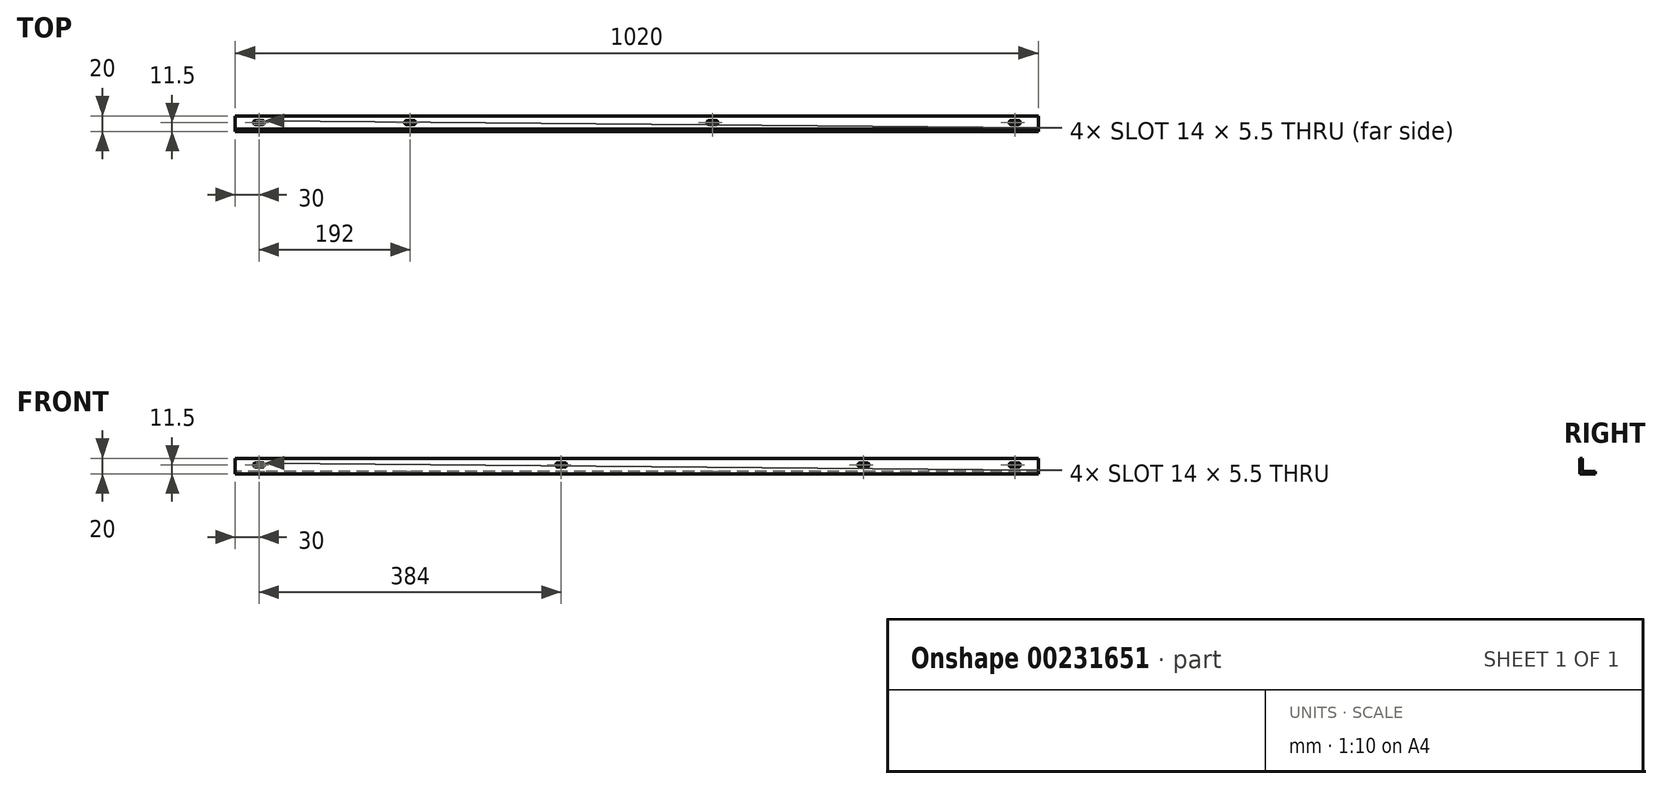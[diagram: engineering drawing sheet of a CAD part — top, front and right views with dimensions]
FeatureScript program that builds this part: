
annotation { "Feature Type Name" : "Feature", "Feature Type Description" : "" }
export const myFeature = defineFeature(function(context is Context, id is Id, definition is map)
    precondition{}
    {
        {
            var Q0;
            Q0=qCreatedBy(makeId("Right.planeOp"),FACE);
            var sketch = newSketch(context, id + "F0", { "sketchPlane" : qUnion([Q0])});
            skLineSegment(sketch, "E0.bottom", {"start": v(0, 0) * mm, "end": v(20, 0) * mm});
            skLineSegment(sketch, "E0.top", {"start": v(3, 3) * mm, "end": v(20, 3) * mm});
            skLineSegment(sketch, "E0.right", {"start": v(20, 0) * mm, "end": v(20, 3) * mm});
            skLineSegment(sketch, "E1.top", {"start": v(0, 20) * mm, "end": v(3, 20) * mm});
            skLineSegment(sketch, "E1.left", {"start": v(0, 0) * mm, "end": v(0, 20) * mm});
            skLineSegment(sketch, "E1.right", {"start": v(3, 3) * mm, "end": v(3, 20) * mm});
            skSolve(sketch);
        }
        {
            var Q0;
            Q0=qSketchRegion(id+"F0",true);
            extrude(context, id + "F1", {"entities" : qUnion([Q0]), "depth" : 1020 * mm});
        }
        {
            var Q0;
            Q0=makeQuery(id+"F1.opExtrude","SWEPT_FACE",FACE,{"disambiguationData":[OSD([sQuery(id+"F0.wireOp",EDGE,"E1.right")])]});
            var sketch = newSketch(context, id + "F2", { "sketchPlane" : qUnion([Q0])});
            skLineSegment(sketch, "E2", {"start": v(-1020, 11.5) * mm, "end": v(0, 11.5) * mm, "construction": true});
            skLineSegment(sketch, "E3.bottom", {"start": v(-994.25, 14.25) * mm, "end": v(-985.75, 14.25) * mm});
            skLineSegment(sketch, "E3.top", {"start": v(-994.25, 8.75) * mm, "end": v(-985.75, 8.75) * mm});
            skArc(sketch, "E4", {"start": v(-994.25, 14.25) * mm, "mid": v(-997, 11.5) * mm, "end": v(-994.25, 8.75) * mm});
            skArc(sketch, "E5", {"start": v(-985.75, 8.75) * mm, "mid": v(-983, 11.5) * mm, "end": v(-985.75, 14.25) * mm});
            skLineSegment(sketch, "E6", {"start": v(-990, 14.25) * mm, "end": v(-990, 8.75) * mm, "construction": true});
            skLineSegment(sketch, "E7.bottom", {"start": v(-34.25, 14.25) * mm, "end": v(-25.75, 14.25) * mm});
            skLineSegment(sketch, "E7.top", {"start": v(-34.25, 8.75) * mm, "end": v(-25.75, 8.75) * mm});
            skArc(sketch, "E8", {"start": v(-34.25, 14.25) * mm, "mid": v(-37, 11.5) * mm, "end": v(-34.25, 8.75) * mm});
            skArc(sketch, "E9", {"start": v(-25.75, 8.75) * mm, "mid": v(-23, 11.5) * mm, "end": v(-25.75, 14.25) * mm});
            skLineSegment(sketch, "E10", {"start": v(-30, 14.25) * mm, "end": v(-30, 8.75) * mm, "construction": true});
            skLineSegment(sketch, "E11.bottom", {"start": v(-802.25, 14.25) * mm, "end": v(-793.75, 14.25) * mm});
            skLineSegment(sketch, "E11.top", {"start": v(-802.25, 8.75) * mm, "end": v(-793.75, 8.75) * mm});
            skArc(sketch, "E12", {"start": v(-802.25, 14.25) * mm, "mid": v(-805, 11.5) * mm, "end": v(-802.25, 8.75) * mm});
            skArc(sketch, "E13", {"start": v(-793.75, 8.75) * mm, "mid": v(-791, 11.5) * mm, "end": v(-793.75, 14.25) * mm});
            skLineSegment(sketch, "E14", {"start": v(-798, 14.25) * mm, "end": v(-798, 8.75) * mm, "construction": true});
            skLineSegment(sketch, "E15.bottom", {"start": v(-418.25, 14.25) * mm, "end": v(-409.75, 14.25) * mm});
            skLineSegment(sketch, "E15.top", {"start": v(-418.25, 8.75) * mm, "end": v(-409.75, 8.75) * mm});
            skArc(sketch, "E16", {"start": v(-418.25, 14.25) * mm, "mid": v(-421, 11.5) * mm, "end": v(-418.25, 8.75) * mm});
            skArc(sketch, "E17", {"start": v(-409.75, 8.75) * mm, "mid": v(-407, 11.5) * mm, "end": v(-409.75, 14.25) * mm});
            skLineSegment(sketch, "E18", {"start": v(-414, 14.25) * mm, "end": v(-414, 8.75) * mm, "construction": true});
            skSolve(sketch);
        }
        {
            var Q0;
            Q0=qSketchRegion(id+"F2",true);
            extrude(context, id + "F3", {"entities" : qUnion([Q0]), "operationType" : NewBodyOperationType.REMOVE, "oppositeDirection" : true, "depth" : 3 * mm});
        }
        {
            var Q0;
            Q0=makeQuery(id+"F1.opExtrude","SWEPT_FACE",FACE,{"disambiguationData":[OSD([sQuery(id+"F0.wireOp",EDGE,"E0.top")])]});
            var sketch = newSketch(context, id + "F4", { "sketchPlane" : qUnion([Q0])});
            skLineSegment(sketch, "E19", {"start": v(0, 11.5) * mm, "end": v(1020, 11.5) * mm, "construction": true});
            skLineSegment(sketch, "E20.bottom", {"start": v(985.75, 14.25) * mm, "end": v(994.25, 14.25) * mm});
            skLineSegment(sketch, "E20.top", {"start": v(985.75, 8.75) * mm, "end": v(994.25, 8.75) * mm});
            skArc(sketch, "E21", {"start": v(985.75, 14.25) * mm, "mid": v(983, 11.5) * mm, "end": v(985.75, 8.75) * mm});
            skArc(sketch, "E22", {"start": v(994.25, 8.75) * mm, "mid": v(997, 11.5) * mm, "end": v(994.25, 14.25) * mm});
            skLineSegment(sketch, "E23", {"start": v(990, 14.25) * mm, "end": v(990, 8.75) * mm, "construction": true});
            skLineSegment(sketch, "E24.bottom", {"start": v(217.75, 14.25) * mm, "end": v(226.25, 14.25) * mm});
            skLineSegment(sketch, "E24.top", {"start": v(217.75, 8.75) * mm, "end": v(226.25, 8.75) * mm});
            skArc(sketch, "E25", {"start": v(217.75, 14.25) * mm, "mid": v(215, 11.5) * mm, "end": v(217.75, 8.75) * mm});
            skArc(sketch, "E26", {"start": v(226.25, 8.75) * mm, "mid": v(229, 11.5) * mm, "end": v(226.25, 14.25) * mm});
            skLineSegment(sketch, "E27", {"start": v(222, 14.25) * mm, "end": v(222, 8.75) * mm, "construction": true});
            skLineSegment(sketch, "E28.bottom", {"start": v(25.75, 14.25) * mm, "end": v(34.25, 14.25) * mm});
            skLineSegment(sketch, "E28.top", {"start": v(25.75, 8.75) * mm, "end": v(34.25, 8.75) * mm});
            skArc(sketch, "E29", {"start": v(25.75, 14.25) * mm, "mid": v(23, 11.5) * mm, "end": v(25.75, 8.75) * mm});
            skArc(sketch, "E30", {"start": v(34.25, 8.75) * mm, "mid": v(37, 11.5) * mm, "end": v(34.25, 14.25) * mm});
            skLineSegment(sketch, "E31", {"start": v(30, 14.25) * mm, "end": v(30, 8.75) * mm, "construction": true});
            skLineSegment(sketch, "E32.bottom", {"start": v(601.75, 14.25) * mm, "end": v(610.25, 14.25) * mm});
            skLineSegment(sketch, "E32.top", {"start": v(601.75, 8.75) * mm, "end": v(610.25, 8.75) * mm});
            skArc(sketch, "E33", {"start": v(601.75, 14.25) * mm, "mid": v(599, 11.5) * mm, "end": v(601.75, 8.75) * mm});
            skArc(sketch, "E34", {"start": v(610.25, 8.75) * mm, "mid": v(613, 11.5) * mm, "end": v(610.25, 14.25) * mm});
            skLineSegment(sketch, "E35", {"start": v(606, 14.25) * mm, "end": v(606, 8.75) * mm, "construction": true});
            skSolve(sketch);
        }
        {
            var Q0;
            Q0=qSketchRegion(id+"F4",true);
            extrude(context, id + "F5", {"entities" : qUnion([Q0]), "operationType" : NewBodyOperationType.REMOVE, "oppositeDirection" : true, "depth" : 3 * mm});
        }
    });
